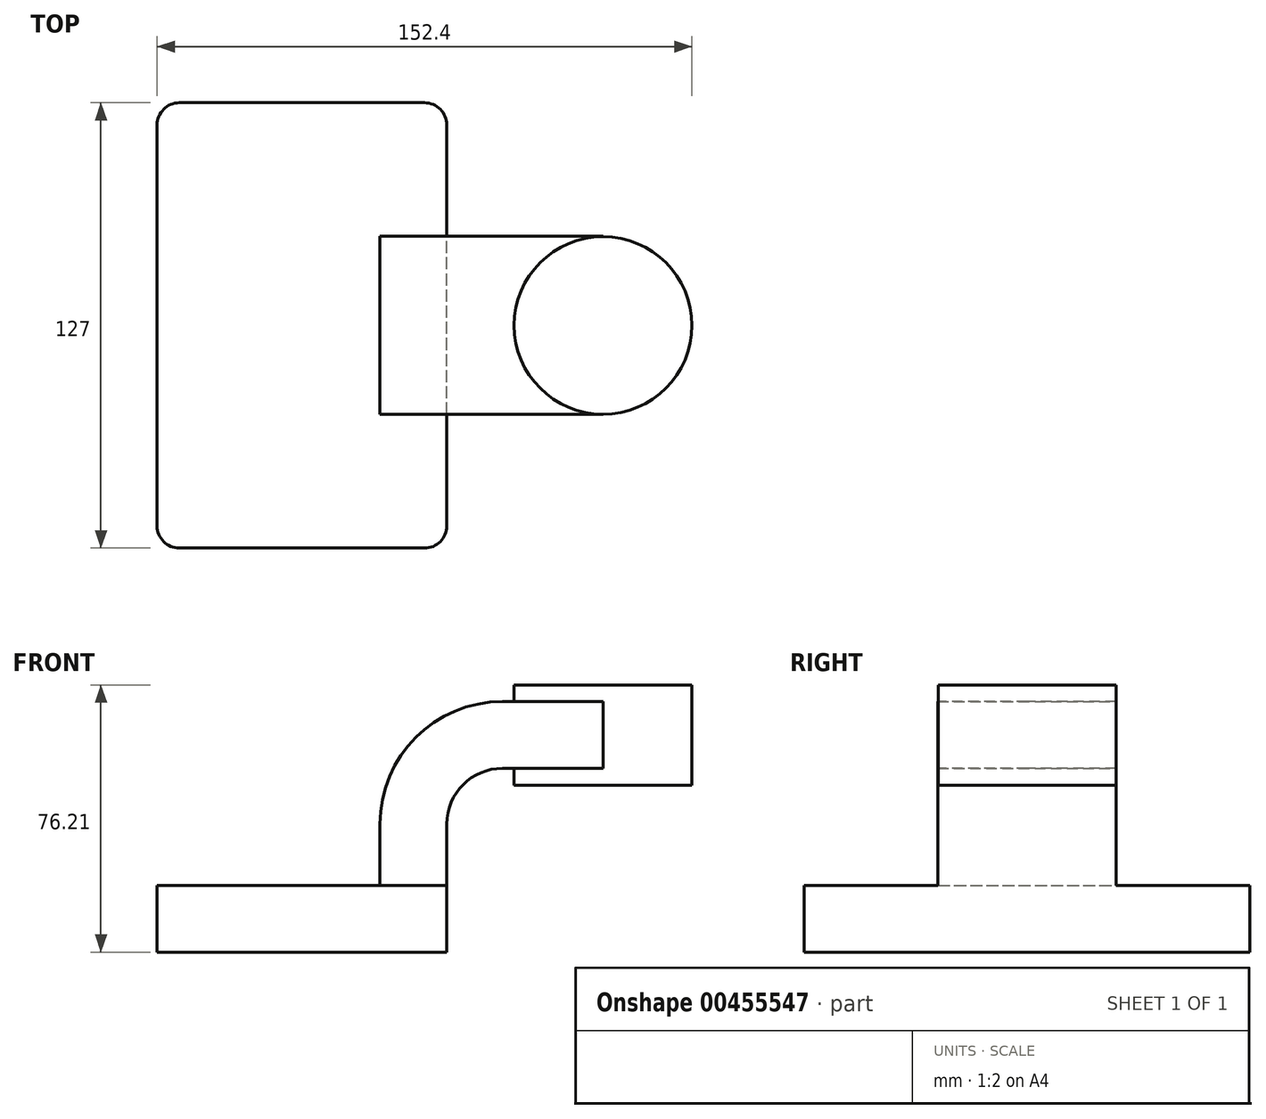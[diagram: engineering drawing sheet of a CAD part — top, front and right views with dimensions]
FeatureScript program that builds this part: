
annotation { "Feature Type Name" : "Feature", "Feature Type Description" : "" }
export const myFeature = defineFeature(function(context is Context, id is Id, definition is map)
    precondition{}
    {
        {
            var Q0;
            Q0=qCreatedBy(makeId("Front.planeOp"),FACE);
            var sketch = newSketch(context, id + "F0", { "sketchPlane" : qUnion([Q0])});
            skLineSegment(sketch, "E0.bottom", {"start": v(-41.28, 9.52) * mm, "end": v(41.28, 9.53) * mm});
            skLineSegment(sketch, "E0.top", {"start": v(-41.28, -9.52) * mm, "end": v(41.28, -9.52) * mm});
            skLineSegment(sketch, "E0.left", {"start": v(-41.28, 9.52) * mm, "end": v(-41.28, -9.53) * mm});
            skLineSegment(sketch, "E0.right", {"start": v(41.28, 9.53) * mm, "end": v(41.28, -9.52) * mm});
            skPoint(sketch, "E0.middle", {"position": v(0, 0) * mm});
            skLineSegment(sketch, "E1.bottom", {"start": v(60.32, 38.1) * mm, "end": v(111.12, 38.1) * mm});
            skLineSegment(sketch, "E1.top", {"start": v(60.32, 66.67) * mm, "end": v(111.12, 66.67) * mm});
            skLineSegment(sketch, "E1.left", {"start": v(60.32, 38.1) * mm, "end": v(60.32, 66.67) * mm});
            skLineSegment(sketch, "E1.right", {"start": v(111.12, 38.1) * mm, "end": v(111.12, 66.67) * mm});
            skPoint(sketch, "E1.middle", {"position": v(85.72, 52.39) * mm});
            skLineSegment(sketch, "E2", {"start": v(41.27, 9.53) * mm, "end": v(41.27, 27) * mm});
            skArc(sketch, "E3", {"start": v(41.27, 27) * mm, "mid": v(45.92, 38.23) * mm, "end": v(57.15, 42.88) * mm});
            skLineSegment(sketch, "E4", {"start": v(57.15, 42.88) * mm, "end": v(85.8, 42.88) * mm});
            skLineSegment(sketch, "E5.0", {"start": v(57.15, 61.93) * mm, "end": v(85.8, 61.93) * mm});
            skArc(sketch, "E5.1", {"start": v(22.22, 27) * mm, "mid": v(32.45, 51.7) * mm, "end": v(57.15, 61.93) * mm});
            skLineSegment(sketch, "E5.2", {"start": v(22.22, 9.53) * mm, "end": v(22.22, 27) * mm});
            skLineSegment(sketch, "E6", {"start": v(85.8, 38.1) * mm, "end": v(85.8, 66.67) * mm});
            skFitSpline(sketch, "E7", {"points": [v(57.15, 61.93) * mm, v(-25.86, 43.04) * mm, v(-41.28, 9.53) * mm], "startDerivative": vector(-209.05, 1.74) * mm, "endDerivative": vector(3.16, -64.05) * mm});
            skSolve(sketch);
        }
        {
            var Q0;
            Q0=makeQuery(id+"F0.imprint","IMPRINT",FACE,{"disambiguationData":[TD([[makeQuery(id+"F0.imprint","IMPRINT",EDGE,{"derivedFrom":sQuery(id+"F0.wireOp",EDGE,"E0.top")}),1.0]])]});
            extrude(context, id + "F1", {"entities" : qUnion([Q0]), "endBound" : BoundingType.SYMMETRIC, "depth" : 127 * mm});
        }
        {
            var Q0;
            {var subQ1=sQuery(id+"F0.wireOp",EDGE,"E2");Q0=makeQuery(id+"F0.imprint","IMPRINT",FACE,{"disambiguationData":[TD([[makeQuery(id+"F0.imprint","IMPRINT",EDGE,{"derivedFrom":subQ1}),1.0]])]});}
            var Q1;
            {var subQ0=sQuery(id+"F0.wireOp",EDGE,"E4");var subQ1=sQuery(id+"F0.wireOp",EDGE,"E1.left");var subQ2=makeQuery(id+"F0.imprint","INTERSECT",VERTEX,{"derivedFrom":[subQ1,subQ0]});Q1=makeQuery(id+"F0.imprint","IMPRINT",FACE,{"disambiguationData":[TD([[makeQuery(id+"F0.imprint","IMPRINT",EDGE,{"disambiguationData":[TD([[subQ2,-1.0]])],"derivedFrom":subQ1}),-1.0]])]});}
            extrude(context, id + "F2", {"entities" : qUnion([Q0, Q1]), "operationType" : NewBodyOperationType.ADD, "endBound" : BoundingType.SYMMETRIC, "depth" : 50.8 * mm});
        }
        {
            var Q0;
            Q0=makeQuery(id+"F0.imprint","IMPRINT",FACE,{"disambiguationData":[TD([[makeQuery(id+"F0.imprint","IMPRINT",EDGE,{"derivedFrom":sQuery(id+"F0.wireOp",EDGE,"E5.1")}),1.0]])]});
            extrude(context, id + "F3", {"entities" : qUnion([Q0]), "operationType" : NewBodyOperationType.ADD, "endBound" : BoundingType.SYMMETRIC, "depth" : 15.88 * mm});
        }
        {
            var Q0;
            {var subQ0=sQuery(id+"F0.wireOp",EDGE,"E1.right");Q0=makeQuery(id+"F0.imprint","IMPRINT",FACE,{"disambiguationData":[TD([[makeQuery(id+"F0.imprint","IMPRINT",EDGE,{"derivedFrom":subQ0}),1.0]])]});}
            var Q1;
            Q1=sQuery(id+"F0.wireOp",EDGE,"E6");
            revolve(context, id + "F4", {"operationType" : NewBodyOperationType.ADD, "entities" : qUnion([Q0]), "axis" : qUnion([Q1]), "revolveType" : RevolveType.FULL});
        }
        {
            var Q0;
            Q0=makeQuery(id+"F1.opExtrude","CAP_EDGE",EDGE,{"disambiguationData":[OSD([sQuery(id+"F0.wireOp",EDGE,"E0.left")])],"isStart":false});
            var Q1;
            Q1=makeQuery(id+"F1.opExtrude","CAP_EDGE",EDGE,{"disambiguationData":[OSD([sQuery(id+"F0.wireOp",EDGE,"E0.right")])],"isStart":false});
            var Q2;
            Q2=makeQuery(id+"F1.opExtrude","CAP_EDGE",EDGE,{"disambiguationData":[OSD([sQuery(id+"F0.wireOp",EDGE,"E0.right")])],"isStart":true});
            var Q3;
            Q3=makeQuery(id+"F1.opExtrude","CAP_EDGE",EDGE,{"disambiguationData":[OSD([sQuery(id+"F0.wireOp",EDGE,"E0.left")])],"isStart":true});
            fillet(context, id + "F5", {"entities" : qUnion([Q0, Q1, Q2, Q3]), "radius" : 6.35 * mm, "tangentPropagation" : true, "allowEdgeOverflow" : false});
        }
    });
